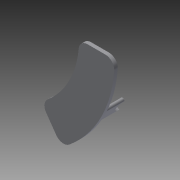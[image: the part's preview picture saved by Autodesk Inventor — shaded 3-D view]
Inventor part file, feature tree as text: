
AUTODESK INVENTOR PART (.ipt)
format: ipt  version: 2014 (Build 180170000, 170)  size: 158,208 bytes
history: native  units: mm
features: extrude x4, sketch x4, projected_geometry x3, fillet x1
ambient origin geometry x8: Origin, YZ Plane, XZ Plane, XY Plane, X Axis, Y Axis, Z Axis, Center Point
bodies: Solid1 (feature_tree)
feature tree (12):
  extrude  "Extrusion1"  Depth=100.0mm
  extrude  "Extrusion2"  Depth=50.0mm
  extrude  "Extrusion3"  Depth=5.0mm
  extrude  "Extrusion4"  Depth=5.0mm
  fillet  "Fillet1"  Radius=2.0mm
  sketch  "Sketch1"  dims[d0=100.0mm d1=100.0mm]
  sketch  "Sketch2"  dims[d2=9.599311mm d3=50.0mm]
  projected_geometry  "Projected Loop1"
  sketch  "Sketch3"  dims[d4=70.0mm d5=5.0mm]
  sketch  "Sketch4"  dims[d6=5.0mm d7=5.0mm d8=2.0mm d9=0.0mm d10=4.799655mm d12=4.0mm d15=10.0mm d16=0.0mm d17=6.0mm d18=0.5mm d19=20.0mm d20=0.0mm d21=2.0mm d22=16.0mm d23=10.0mm d24=0.0mm d25=1.0mm]
  projected_geometry  "Projected Loop2"
  projected_geometry  "Projected Loop3"
